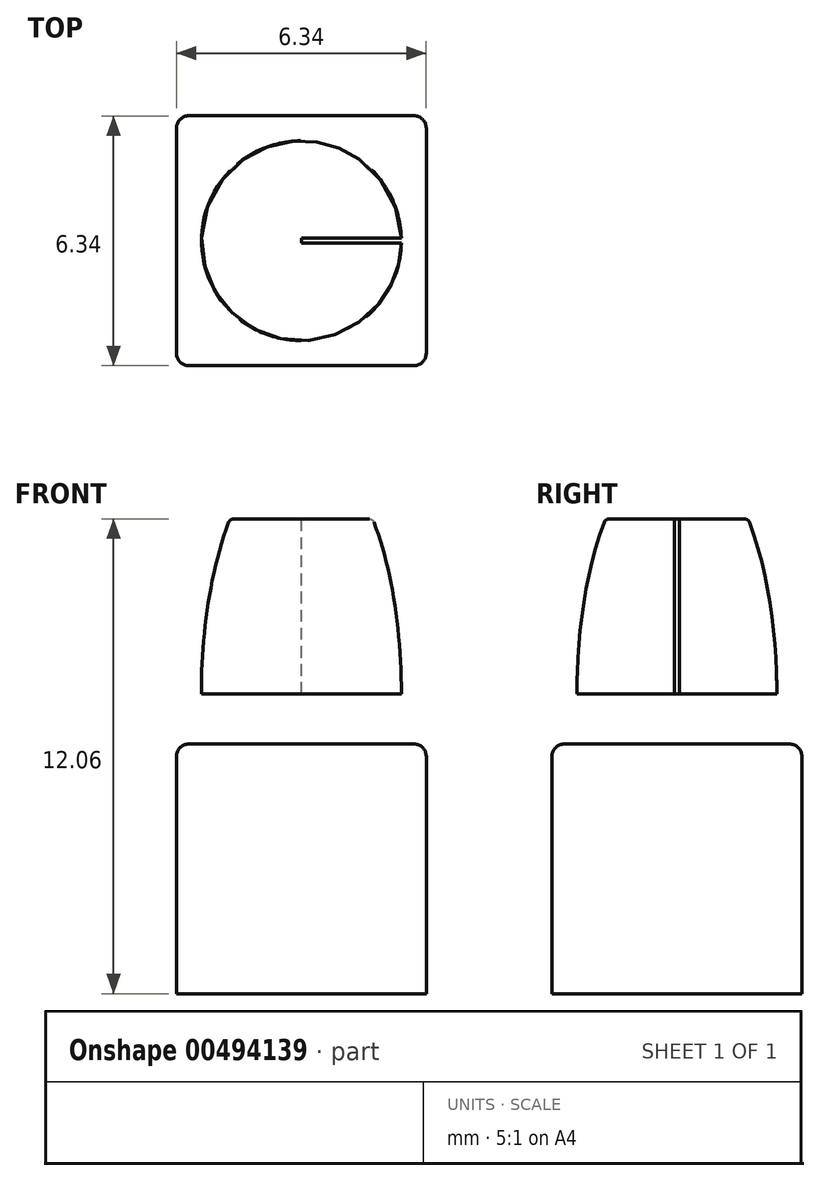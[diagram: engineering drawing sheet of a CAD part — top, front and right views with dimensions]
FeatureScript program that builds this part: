
annotation { "Feature Type Name" : "Feature", "Feature Type Description" : "" }
export const myFeature = defineFeature(function(context is Context, id is Id, definition is map)
    precondition{}
    {
        {
            var Q0;
            Q0=qCreatedBy(makeId("Top.planeOp"),FACE);
            var sketch = newSketch(context, id + "F0", { "sketchPlane" : qUnion([Q0])});
            skLineSegment(sketch, "E0.bottom", {"start": v(-2.86, 3.17) * mm, "end": v(2.86, 3.17) * mm});
            skLineSegment(sketch, "E0.top", {"start": v(-2.86, -3.18) * mm, "end": v(2.86, -3.18) * mm});
            skLineSegment(sketch, "E0.left", {"start": v(-3.17, 2.86) * mm, "end": v(-3.18, -2.86) * mm});
            skLineSegment(sketch, "E0.right", {"start": v(3.18, 2.86) * mm, "end": v(3.17, -2.86) * mm});
            skPoint(sketch, "E0.middle", {"position": v(0, 0) * mm});
            skPoint(sketch, "E1.visualSharp", {"position": v(-3.17, 3.17) * mm});
            skArc(sketch, "E1.filletArc", {"start": v(-2.86, 3.17) * mm, "mid": v(-3.08, 3.08) * mm, "end": v(-3.17, 2.86) * mm});
            skPoint(sketch, "E2.visualSharp", {"position": v(-3.18, -3.18) * mm});
            skArc(sketch, "E2.filletArc", {"start": v(-3.18, -2.86) * mm, "mid": v(-3.08, -3.08) * mm, "end": v(-2.86, -3.18) * mm});
            skPoint(sketch, "E3.visualSharp", {"position": v(3.17, -3.18) * mm});
            skArc(sketch, "E3.filletArc", {"start": v(2.86, -3.18) * mm, "mid": v(3.08, -3.08) * mm, "end": v(3.17, -2.86) * mm});
            skPoint(sketch, "E4.visualSharp", {"position": v(3.18, 3.17) * mm});
            skArc(sketch, "E4.filletArc", {"start": v(3.18, 2.86) * mm, "mid": v(3.08, 3.08) * mm, "end": v(2.86, 3.17) * mm});
            skSolve(sketch);
        }
        {
            var Q0;
            Q0=qSketchRegion(id+"F0",true);
            extrude(context, id + "F1", {"entities" : qUnion([Q0]), "endBound" : BoundingType.SYMMETRIC, "depth" : 6.35 * mm});
        }
        {
            var Q0;
            Q0=makeQuery(id+"F1.opExtrude","CAP_EDGE",EDGE,{"disambiguationData":[OSD([sQuery(id+"F0.wireOp",EDGE,"E0.bottom")])],"isStart":false});
            fillet(context, id + "F2", {"entities" : qUnion([Q0]), "radius" : 0.32 * mm, "tangentPropagation" : true, "allowEdgeOverflow" : false});
        }
        {
            var Q0;
            Q0=qCreatedBy(makeId("Front.planeOp"),FACE);
            var sketch = newSketch(context, id + "F3", { "sketchPlane" : qUnion([Q0])});
            skArc(sketch, "E5.0.0", {"start": v(-2.86, 3.18) * mm, "mid": v(-3.08, 3.08) * mm, "end": v(-3.18, 2.86) * mm});
            skArc(sketch, "E5.0.2", {"start": v(-3.18, 2.86) * mm, "mid": v(-3.08, 3.08) * mm, "end": v(-2.86, 3.18) * mm});
            skLineSegment(sketch, "E6.0.1", {"start": v(-2.86, 3.18) * mm, "end": v(2.86, 3.18) * mm});
            skLineSegment(sketch, "E6.0.3", {"start": v(2.86, 3.18) * mm, "end": v(-2.86, 3.18) * mm});
            skArc(sketch, "E7.0.0", {"start": v(3.17, 2.86) * mm, "mid": v(3.08, 3.08) * mm, "end": v(2.86, 3.18) * mm});
            skArc(sketch, "E7.0.2", {"start": v(2.86, 3.18) * mm, "mid": v(3.08, 3.08) * mm, "end": v(3.17, 2.86) * mm});
            skLineSegment(sketch, "E8", {"start": v(0, 3.18) * mm, "end": v(0, 8.9) * mm});
            skPoint(sketch, "E8.endSnap0", {"position": v(0, 3.18) * mm});
            skLineSegment(sketch, "E9", {"start": v(0, 8.9) * mm, "end": v(1.81, 8.9) * mm});
            skLineSegment(sketch, "E10.bottom", {"start": v(0, 3.18) * mm, "end": v(2.54, 3.18) * mm});
            skLineSegment(sketch, "E10.top", {"start": v(0, 4.45) * mm, "end": v(2.54, 4.45) * mm});
            skLineSegment(sketch, "E10.left", {"start": v(0, 3.18) * mm, "end": v(0, 4.45) * mm});
            skLineSegment(sketch, "E10.right", {"start": v(2.54, 3.18) * mm, "end": v(2.54, 4.45) * mm});
            skLineSegment(sketch, "E11.0.0", {"start": v(-3.18, -3.17) * mm, "end": v(-3.18, 2.86) * mm});
            skLineSegment(sketch, "E11.0.2", {"start": v(-3.17, 2.86) * mm, "end": v(-3.17, -3.17) * mm});
            skLineSegment(sketch, "E12.0.0", {"start": v(3.18, -3.17) * mm, "end": v(3.18, 2.86) * mm});
            skLineSegment(sketch, "E12.0.2", {"start": v(3.17, 2.86) * mm, "end": v(3.17, -3.17) * mm});
            skLineSegment(sketch, "E13.0.0", {"start": v(-2.86, -3.18) * mm, "end": v(-3.18, -3.18) * mm});
            skLineSegment(sketch, "E13.0.2", {"start": v(-3.17, -3.18) * mm, "end": v(-2.86, -3.18) * mm});
            skLineSegment(sketch, "E13.0.3", {"start": v(-2.86, -3.18) * mm, "end": v(2.86, -3.18) * mm});
            skLineSegment(sketch, "E13.0.4", {"start": v(2.86, -3.18) * mm, "end": v(3.18, -3.18) * mm});
            skLineSegment(sketch, "E13.0.6", {"start": v(3.17, -3.18) * mm, "end": v(2.86, -3.18) * mm});
            skLineSegment(sketch, "E13.0.7", {"start": v(2.86, -3.18) * mm, "end": v(-2.86, -3.18) * mm});
            skEllipticalArc(sketch, "E14", {});
            skFitSpline(sketch, "E15.0", {"points": [v(0.32, 10.37) * mm, v(0, 10.44) * mm, v(-0.32, 10.37) * mm, v(-0.7, 10.09) * mm, v(-1.1, 9.56) * mm, v(-1.45, 8.82) * mm, v(-1.76, 7.9) * mm, v(-1.99, 6.83) * mm, v(-2.13, 5.66) * mm, v(-2.18, 4.45) * mm, v(-2.13, 3.23) * mm, v(-1.99, 2.06) * mm, v(-1.76, 0.99) * mm, v(-1.45, 0.07) * mm, v(-1.1, -0.67) * mm, v(-0.7, -1.2) * mm, v(-0.32, -1.48) * mm, v(0, -1.55) * mm, v(0.32, -1.48) * mm, v(0.7, -1.2) * mm, v(1.1, -0.67) * mm, v(1.45, 0.07) * mm, v(1.76, 0.99) * mm, v(1.99, 2.06) * mm, v(2.13, 3.23) * mm, v(2.18, 4.45) * mm, v(2.13, 5.66) * mm, v(1.99, 6.83) * mm, v(1.76, 7.9) * mm, v(1.45, 8.82) * mm, v(1.1, 9.56) * mm, v(0.7, 10.09) * mm, v(0.32, 10.37) * mm, v(0, 10.44) * mm, v(-0.32, 10.37) * mm]});
            skFitSpline(sketch, "E16.0", {"points": [v(0.44, 10.6) * mm, v(0, 10.7) * mm, v(-0.44, 10.6) * mm, v(-0.88, 10.26) * mm, v(-1.31, 9.7) * mm, v(-1.69, 8.92) * mm, v(-2, 7.97) * mm, v(-2.24, 6.87) * mm, v(-2.38, 5.68) * mm, v(-2.43, 4.45) * mm, v(-2.38, 3.2) * mm, v(-2.24, 2.02) * mm, v(-2, 0.92) * mm, v(-1.69, -0.03) * mm, v(-1.31, -0.8) * mm, v(-0.88, -1.37) * mm, v(-0.44, -1.7) * mm, v(0, -1.81) * mm, v(0.44, -1.7) * mm, v(0.88, -1.37) * mm, v(1.31, -0.8) * mm, v(1.69, -0.03) * mm, v(2, 0.92) * mm, v(2.24, 2.02) * mm, v(2.38, 3.2) * mm, v(2.43, 4.45) * mm, v(2.38, 5.68) * mm, v(2.24, 6.87) * mm, v(2, 7.97) * mm, v(1.69, 8.92) * mm, v(1.31, 9.7) * mm, v(0.88, 10.26) * mm, v(0.44, 10.6) * mm, v(0, 10.7) * mm, v(-0.44, 10.6) * mm]});
            skLineSegment(sketch, "E17", {"start": v(1.7, 8.84) * mm, "end": v(1.68, 8.9) * mm});
            skLineSegment(sketch, "E18", {"start": v(1.46, 8.75) * mm, "end": v(1.46, 8.9) * mm});
            const initialGuessF3  = {"E14": [0, 0.004445, 0, 1, 0.00635, 0.00254, 4.71238898038469, 5.487786476995442]};
            skSetInitialGuess(sketch, initialGuessF3);
            skSolve(sketch);
        }
        {
            var Q0;
            Q0=makeQuery(id+"F3.imprint","IMPRINT",FACE,{"disambiguationData":[TD([[makeQuery(id+"F3.imprint","IMPRINT",EDGE,{"derivedFrom":sQuery(id+"F3.wireOp",EDGE,"E10.bottom")}),1.0]])]});
            var Q1;
            {var subQ0=sQuery(id+"F3.wireOp",EDGE,"45745adf-f94e-404d-bc12-fde483d5a78a.0");Q1=makeQuery(id+"F3.imprint","IMPRINT",FACE,{"disambiguationData":[TD([[makeQuery(id+"F3.imprint","IMPRINT",EDGE,{"derivedFrom":subQ0}),-1.0]])]});}
            var Q2;
            {var subQ0=sQuery(id+"F3.wireOp",EDGE,"AdALbvXk-3wPX-6Fpe-rOfn-Via4XpPnjhGq");Q2=makeQuery(id+"F3.imprint","IMPRINT",FACE,{"disambiguationData":[TD([[makeQuery(id+"F3.imprint","IMPRINT",EDGE,{"derivedFrom":subQ0}),1.0]])]});}
            var Q3;
            {var subQ0=sQuery(id+"F3.wireOp",EDGE,"E15.0");Q3=makeQuery(id+"F3.imprint","IMPRINT",FACE,{"disambiguationData":[TD([[makeQuery(id+"F3.imprint","IMPRINT",EDGE,{"derivedFrom":subQ0}),-1.0]])]});}
            var Q4;
            {var subQ0=sQuery(id+"F3.wireOp",EDGE,"E14");Q4=makeQuery(id+"F3.imprint","IMPRINT",FACE,{"disambiguationData":[TD([[makeQuery(id+"F3.imprint","IMPRINT",EDGE,{"derivedFrom":subQ0}),1.0]])]});}
            var Q5;
            Q5=sQuery(id+"F3.wireOp",EDGE,"E8");
            revolve(context, id + "F4", {"operationType" : NewBodyOperationType.ADD, "entities" : qUnion([Q0, Q1, Q2, Q3, Q4]), "axis" : qUnion([Q5]), "revolveType" : RevolveType.FULL});
        }
        {
            var Q0;
            Q0=makeQuery(id+"F4.opRevolve","SWEPT_EDGE",EDGE,{"disambiguationData":[OSD([sQuery(id+"F3.wireOp",EDGE,"E9"),sQuery(id+"F3.wireOp",EDGE,"E14")])]});
            fillet(context, id + "F5", {"entities" : qUnion([Q0]), "radius" : 0.13 * mm, "tangentPropagation" : true, "allowEdgeOverflow" : false});
        }
        {
            var Q0;
            {var subQ0=sQuery(id+"F3.wireOp",EDGE,"E14");Q0=makeQuery(id+"F3.imprint","IMPRINT",FACE,{"disambiguationData":[TD([[makeQuery(id+"F3.imprint","IMPRINT",EDGE,{"derivedFrom":subQ0}),1.0]])]});}
            extrude(context, id + "F6", {"entities" : qUnion([Q0]), "operationType" : NewBodyOperationType.REMOVE, "endBound" : BoundingType.SYMMETRIC, "depth" : 0.13 * mm});
        }
    });
